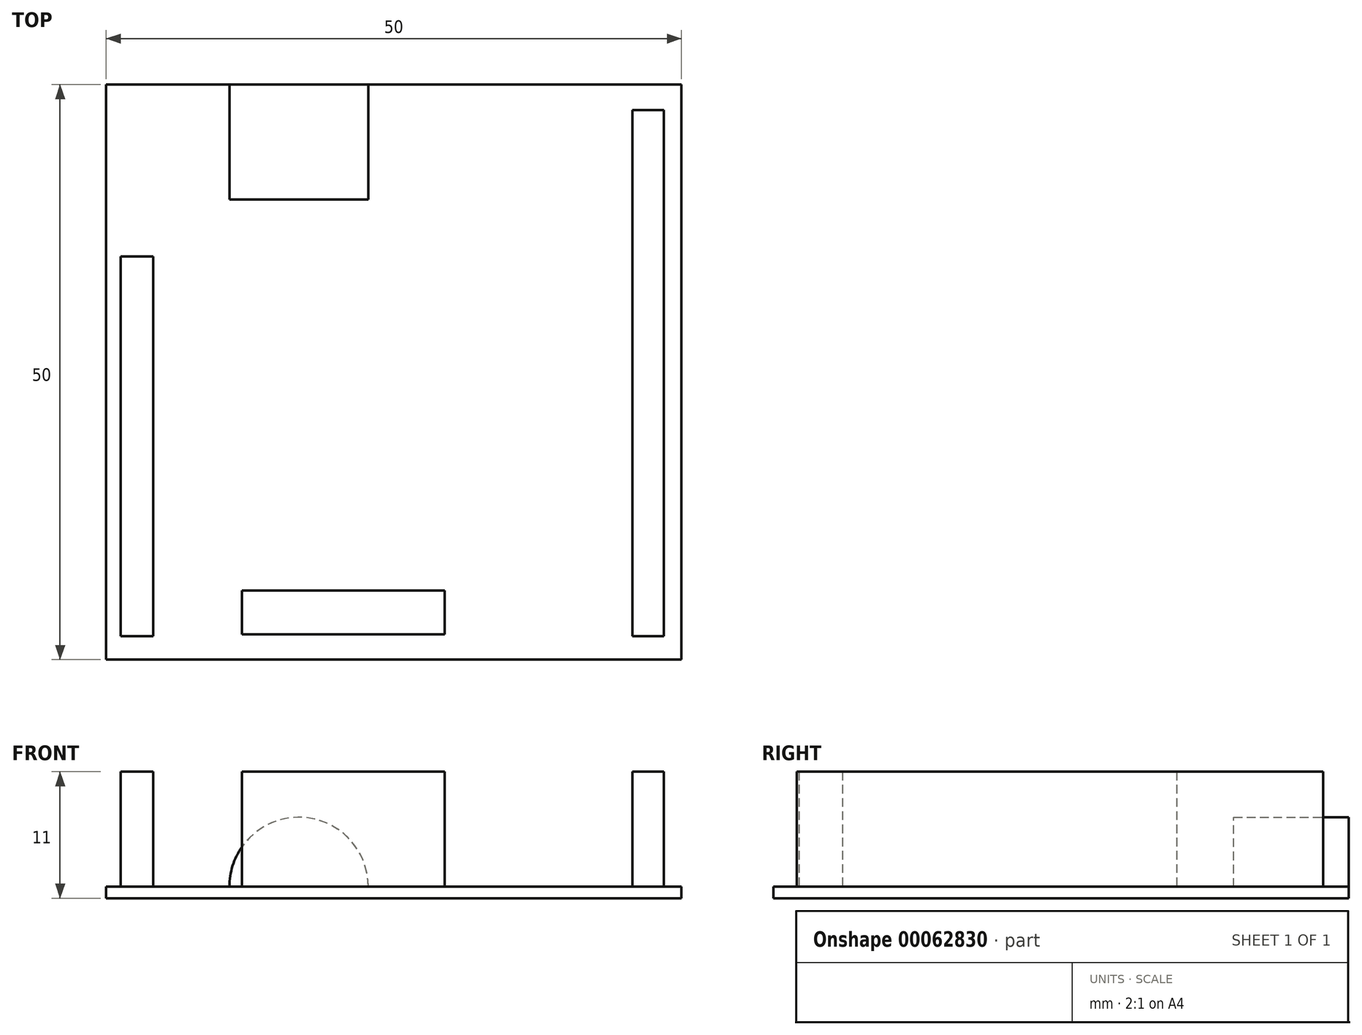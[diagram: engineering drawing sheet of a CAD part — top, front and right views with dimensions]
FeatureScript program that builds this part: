
annotation { "Feature Type Name" : "Feature", "Feature Type Description" : "" }
export const myFeature = defineFeature(function(context is Context, id is Id, definition is map)
    precondition{}
    {
        {
            var Q0;
            Q0=qCreatedBy(makeId("Top.planeOp"),FACE);
            var sketch = newSketch(context, id + "F0", { "sketchPlane" : qUnion([Q0])});
            skLineSegment(sketch, "E0.rect.bottom", {"start": v(25, 25) * mm, "end": v(-25, 25) * mm});
            skLineSegment(sketch, "E0.rect.top", {"start": v(25, -25) * mm, "end": v(-25, -25) * mm});
            skLineSegment(sketch, "E0.rect.left", {"start": v(25, 25) * mm, "end": v(25, -25) * mm});
            skLineSegment(sketch, "E0.rect.right", {"start": v(-25, 25) * mm, "end": v(-25, -25) * mm});
            skPoint(sketch, "E0.rect.middle", {"position": v(0, 0) * mm});
            skSolve(sketch);
        }
        {
            var Q0;
            Q0=makeQuery(id+"F0.imprint","IMPRINT",FACE,{"disambiguationData":[TD([[makeQuery(id+"F0.imprint","IMPRINT",EDGE,{"derivedFrom":sQuery(id+"F0.wireOp",EDGE,"E0.rect.bottom")}),1.0]])]});
            extrude(context, id + "F1", {"entities" : qUnion([Q0]), "depth" : 1 * mm});
        }
        {
            var Q0;
            Q0=makeQuery(id+"F1.opExtrude","CAP_FACE",FACE,{"disambiguationData":[OSD([sQuery(id+"F0.wireOp",EDGE,"E0.rect.bottom"),sQuery(id+"F0.wireOp",EDGE,"E0.rect.top"),sQuery(id+"F0.wireOp",EDGE,"E0.rect.left"),sQuery(id+"F0.wireOp",EDGE,"E0.rect.right")])],"isStart":false});
            var sketch = newSketch(context, id + "F2", { "sketchPlane" : qUnion([Q0])});
            skLineSegment(sketch, "E1.bottom", {"start": v(23.46, -22.97) * mm, "end": v(20.74, -22.97) * mm});
            skLineSegment(sketch, "E1.top", {"start": v(23.46, 22.8) * mm, "end": v(20.74, 22.8) * mm});
            skLineSegment(sketch, "E1.left", {"start": v(23.46, -22.97) * mm, "end": v(23.46, 22.8) * mm});
            skLineSegment(sketch, "E1.right", {"start": v(20.74, -22.97) * mm, "end": v(20.74, 22.8) * mm});
            skSolve(sketch);
        }
        {
            var Q0;
            Q0=makeQuery(id+"F2.imprint","IMPRINT",FACE,{"disambiguationData":[TD([[makeQuery(id+"F2.imprint","IMPRINT",EDGE,{"derivedFrom":sQuery(id+"F2.wireOp",EDGE,"E1.bottom")}),-1.0]])]});
            var Q1;
            Q1=sQuery(id+"F2.wireOp",EDGE,"E1.right");
            extrude(context, id + "F3", {"entities" : qUnion([Q0]), "operationType" : NewBodyOperationType.ADD, "surfaceEntities" : qUnion([Q1]), "depth" : 10 * mm});
        }
        {
            var Q0;
            Q0=makeQuery(id+"F1.opExtrude","CAP_FACE",FACE,{"disambiguationData":[OSD([sQuery(id+"F0.wireOp",EDGE,"E0.rect.bottom"),sQuery(id+"F0.wireOp",EDGE,"E0.rect.top"),sQuery(id+"F0.wireOp",EDGE,"E0.rect.left"),sQuery(id+"F0.wireOp",EDGE,"E0.rect.right")])],"isStart":false});
            var sketch = newSketch(context, id + "F4", { "sketchPlane" : qUnion([Q0])});
            skLineSegment(sketch, "E2.bottom", {"start": v(-23.74, -22.95) * mm, "end": v(-20.92, -22.95) * mm});
            skLineSegment(sketch, "E2.top", {"start": v(-23.74, 10.05) * mm, "end": v(-20.92, 10.05) * mm});
            skLineSegment(sketch, "E2.left", {"start": v(-23.74, -22.95) * mm, "end": v(-23.74, 10.05) * mm});
            skLineSegment(sketch, "E2.right", {"start": v(-20.92, -22.95) * mm, "end": v(-20.92, 10.05) * mm});
            skSolve(sketch);
        }
        {
            var Q0;
            Q0=makeQuery(id+"F4.imprint","IMPRINT",FACE,{"disambiguationData":[TD([[makeQuery(id+"F4.imprint","IMPRINT",EDGE,{"derivedFrom":sQuery(id+"F4.wireOp",EDGE,"E2.bottom")}),1.0]])]});
            extrude(context, id + "F5", {"entities" : qUnion([Q0]), "operationType" : NewBodyOperationType.ADD, "depth" : 10 * mm});
        }
        {
            var Q0;
            Q0=makeQuery(id+"F1.opExtrude","CAP_FACE",FACE,{"disambiguationData":[OSD([sQuery(id+"F0.wireOp",EDGE,"E0.rect.bottom"),sQuery(id+"F0.wireOp",EDGE,"E0.rect.top"),sQuery(id+"F0.wireOp",EDGE,"E0.rect.left"),sQuery(id+"F0.wireOp",EDGE,"E0.rect.right")])],"isStart":false});
            var sketch = newSketch(context, id + "F6", { "sketchPlane" : qUnion([Q0])});
            skLineSegment(sketch, "E3.bottom", {"start": v(-13.2, -22.8) * mm, "end": v(4.43, -22.8) * mm});
            skLineSegment(sketch, "E3.top", {"start": v(-13.2, -19) * mm, "end": v(4.43, -19) * mm});
            skLineSegment(sketch, "E3.left", {"start": v(-13.2, -22.8) * mm, "end": v(-13.2, -19) * mm});
            skLineSegment(sketch, "E3.right", {"start": v(4.43, -22.8) * mm, "end": v(4.43, -19) * mm});
            skSolve(sketch);
        }
        {
            var Q0;
            Q0=makeQuery(id+"F6.imprint","IMPRINT",FACE,{"disambiguationData":[TD([[makeQuery(id+"F6.imprint","IMPRINT",EDGE,{"derivedFrom":sQuery(id+"F6.wireOp",EDGE,"E3.bottom")}),1.0]])]});
            var Q1;
            Q1=sQuery(id+"F6.wireOp",EDGE,"E3.top");
            extrude(context, id + "F7", {"entities" : qUnion([Q0]), "operationType" : NewBodyOperationType.ADD, "surfaceEntities" : qUnion([Q1]), "depth" : 10 * mm});
        }
        {
            var Q0;
            Q0=makeQuery(id+"F1.opExtrude","SWEPT_FACE",FACE,{"disambiguationData":[OSD([sQuery(id+"F0.wireOp",EDGE,"E0.rect.bottom")])]});
            var sketch = newSketch(context, id + "F8", { "sketchPlane" : qUnion([Q0])});
            skArc(sketch, "E4", {"start": v(14.3, 1) * mm, "mid": v(8.26, 7.03) * mm, "end": v(2.22, 1) * mm});
            skLineSegment(sketch, "E5", {"start": v(2.22, 1) * mm, "end": v(14.3, 1) * mm});
            skSolve(sketch);
        }
        {
            var Q0;
            Q0 = qSketchRegion(id + "F8", true);
            extrude(context, id + "F9", {"entities" : qUnion([Q0]), "operationType" : NewBodyOperationType.ADD, "oppositeDirection" : true, "depth" : 10 * mm});
        }
    });
